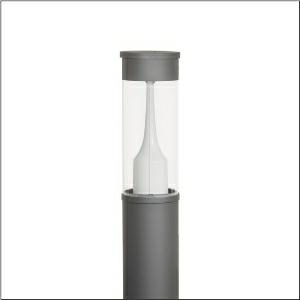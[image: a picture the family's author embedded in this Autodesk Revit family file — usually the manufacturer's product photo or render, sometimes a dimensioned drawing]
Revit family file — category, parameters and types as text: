
# Revit family: city-light_260_iq___p1_0a_5xa5295bf14h_d7c3
name_source: partatom
category: Lighting Fixtures
units: mm (PartAtom-declared; Revit-internal decimal feet)

## family parameters
Cut with Voids When Loaded = No
Host = Face
Light Source = No
Part Type = Normal
Room Calculation Point = No
Round Connector Dimension = Use Diameter
Shared = No

## types (1)
- --- (1 x LED, 1510 lm, 12.9 W, 2200K)
    Apparent Load = 13 VA
    CIE Flux Codes = 32 61 90 93 100
    Color Rendering = 70
    Color Temperature = 2200K
    Default Elevation = 1800 mm
    Description = City-Light 260 iQ, light pillar, Module 540 iQ-SR, primary light control with 3 zone facetted reflector, of plastic, silver coated, highly specular, structured, primary optical cover: cover, of PMMA, transparent, partly coated, light distribution: P1.0a, primary light characteristic: strongly asymmetric, LED, High Power LED, rated luminous flux: 1.510lm, luminous efficacy: 117lm/W, light colour: 722, colour temperature: 2200K, control gear: ECG iQ, control: presetting dimming logarithmic, Street-Remote, Auto-Match, Temp-Guard, Lumen-Switch, Night-Set, Smart-Wire, Light-Fading, Desk-Remote (wireless, voltage-free reading and setting of iQ features in the workshop via application-optimized NFC function/RFID function), optimised constant luminous flux control (CLO 2.0), with terminal, 6-pole, max. 2.5mm², mains connection: 220..240V, AC, 50/60Hz, start of lifetime: 13W, end of lifetime: 13W, reduction: 6W, luminaire housing, cylindrical, of extruded aluminium section, coated, Siteco® metallic grey (DB 702S), length: 2.600mm, diameter: 200mm, Module 540 iQ-SR, traffic white (RAL 9016), equipment: standard, protection rating (complete): IP65, insulation class (complete): insulation class II (safety insulation), certification: CE, ENEC, VDE, packaging unit: 1 piece

Light Distribution: P1.0a
    Height = 500 mm
    Lamp = 1 x LED
    Lamp Light Flux = 1510 lm
    Lamp Power = 12.9 W
    Lamp count = 1
    Length = 200 mm  [stored 0.656168 ft]
    Luminous efficacy = 117 lm/W
    Manufacturer = Siteco
    ModVariant = No
    Model = 5XA5295BF14H
    Number of Poles = 1
    OnlyDefault = Yes
    Power Factor = 1
    Product Name = City-Light 260 iQ | P1.0a
    Product group = light pillar | pylon top
    ProductGroupID = 6103
    Protection Class = Protection class II
    Protection Degree = IP 65
    RLX_Detail_Level = 1
    RlxData = <blob elided: 52957 chars, md5=2bbd1081>
    Socket = socket
    Standby Power = 0 W
    System Light Flux = 1510 lm
    System Power = 13 W
    Type Comments = factory setting: luminous flux: 100 % | dim-lin: 254 | 516 mA
    Type Image = l_1006918.jpg
    URL = http://relux.com
    VarID = @adj_070775
    Voltage = 0 V
    Weight = 0.00 kg
    Width = 0 mm  [stored 0 ft]

note: [stored X ft] marks values corroborated as IEEE doubles in the binary element streams (Revit-internal decimal feet)

## geometry (parser evidence)
native form markers: Blend x4, Sweep x10
no freeform markers — native parametric forms only
